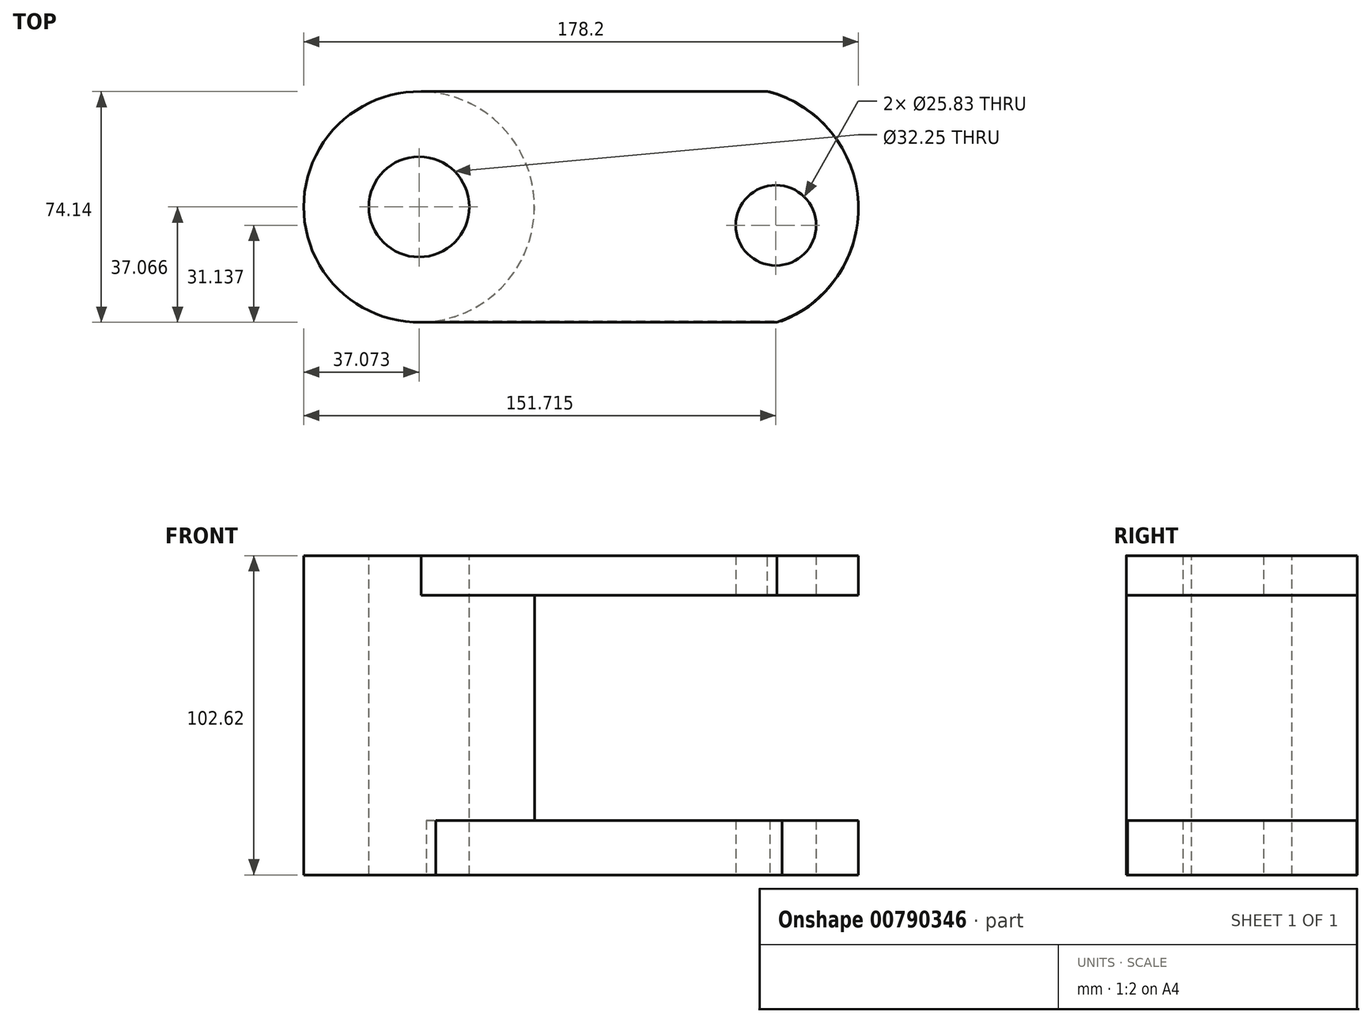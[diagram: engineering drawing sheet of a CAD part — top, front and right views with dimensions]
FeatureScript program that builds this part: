
annotation { "Feature Type Name" : "Feature", "Feature Type Description" : "" }
export const myFeature = defineFeature(function(context is Context, id is Id, definition is map)
    precondition{}
    {
        {
            var Q0;
            Q0=qCreatedBy(makeId("Top.planeOp"),FACE);
            var sketch = newSketch(context, id + "F0", { "sketchPlane" : qUnion([Q0])});
            skCircle(sketch, "E0", {"center": v(-39.45, -5.96) * mm, "radius": 37.07 * mm});
            skSolve(sketch);
        }
        {
            var Q0;
            Q0=makeQuery(id+"F0.imprint","IMPRINT",FACE,{"disambiguationData":[TD([[makeQuery(id+"F0.imprint","IMPRINT",EDGE,{"derivedFrom":sQuery(id+"F0.wireOp",EDGE,"E0")}),1.0]])]});
            extrude(context, id + "F1", {"entities" : qUnion([Q0]), "depth" : 102.62 * mm, "offsetDistance" : 25.4 * mm});
        }
        {
            var Q0;
            Q0=makeQuery(id+"F1.opExtrude","CAP_FACE",FACE,{"disambiguationData":[OSD([sQuery(id+"F0.wireOp",EDGE,"E0")])],"isStart":false});
            var sketch = newSketch(context, id + "F2", { "sketchPlane" : qUnion([Q0])});
            skCircle(sketch, "E1", {"center": v(-39.45, -5.96) * mm, "radius": 16.13 * mm});
            skSolve(sketch);
        }
        {
            var Q0;
            Q0=makeQuery(id+"F2.imprint","IMPRINT",FACE,{"disambiguationData":[TD([[makeQuery(id+"F2.imprint","IMPRINT",EDGE,{"derivedFrom":sQuery(id+"F2.wireOp",EDGE,"E1")}),1.0]])]});
            extrude(context, id + "F3", {"entities" : qUnion([Q0]), "operationType" : NewBodyOperationType.REMOVE, "oppositeDirection" : true, "depth" : 147.83 * mm, "offsetDistance" : 25.4 * mm});
        }
        {
            var Q0;
            Q0=makeQuery(id+"F1.opExtrude","CAP_FACE",FACE,{"disambiguationData":[OSD([sQuery(id+"F0.wireOp",EDGE,"E0")])],"isStart":false});
            var sketch = newSketch(context, id + "F4", { "sketchPlane" : qUnion([Q0])});
            skLineSegment(sketch, "E2", {"start": v(-40.11, 31.1) * mm, "end": v(72.5, 31.1) * mm});
            skLineSegment(sketch, "E3", {"start": v(-40.11, -43.03) * mm, "end": v(75.53, -43.03) * mm});
            skArc(sketch, "E4", {"start": v(75.53, -43.03) * mm, "mid": v(101.65, -4.84) * mm, "end": v(72.5, 31.1) * mm});
            skSolve(sketch);
        }
        {
            var Q0;
            {var subQ0=sQuery(id+"F4.wireOp",EDGE,"E4");Q0=makeQuery(id+"F4.imprint","IMPRINT",FACE,{"disambiguationData":[TD([[makeQuery(id+"F4.imprint","IMPRINT",EDGE,{"derivedFrom":subQ0}),1.0]])]});}
            extrude(context, id + "F5", {"entities" : qUnion([Q0]), "operationType" : NewBodyOperationType.ADD, "oppositeDirection" : true, "depth" : 12.7 * mm, "offsetDistance" : 25.4 * mm});
        }
        {
            var Q0;
            Q0=makeQuery(id+"F1.opExtrude","CAP_FACE",FACE,{"disambiguationData":[OSD([sQuery(id+"F0.wireOp",EDGE,"E0")])],"isStart":true});
            var sketch = newSketch(context, id + "F6", { "sketchPlane" : qUnion([Q0])});
            skLineSegment(sketch, "E5", {"start": v(-34.13, 42.65) * mm, "end": v(77.21, 42.65) * mm});
            skLineSegment(sketch, "E6", {"start": v(-37.13, -31.03) * mm, "end": v(73.18, -31.03) * mm});
            skArc(sketch, "E7", {"start": v(73.18, -31.03) * mm, "mid": v(101.6, 4.36) * mm, "end": v(77.21, 42.65) * mm});
            skSolve(sketch);
        }
        {
            var Q0;
            {var subQ0=sQuery(id+"F6.wireOp",EDGE,"E5");Q0=makeQuery(id+"F6.imprint","IMPRINT",FACE,{"disambiguationData":[TD([[makeQuery(id+"F6.imprint","IMPRINT",EDGE,{"derivedFrom":subQ0}),-1.0]])]});}
            extrude(context, id + "F7", {"entities" : qUnion([Q0]), "operationType" : NewBodyOperationType.ADD, "oppositeDirection" : true, "depth" : 17.53 * mm, "offsetDistance" : 25.4 * mm});
        }
        {
            var Q0;
            {var subQ0=sQuery(id+"F0.wireOp",EDGE,"E0");Q0=makeQuery(id+"F7.boolean.opBoolean","MERGE",FACE,{"derivedFrom":[makeQuery(id+"F1.opExtrude","CAP_FACE",FACE,{"disambiguationData":[OSD([subQ0])],"isStart":true}),makeQuery(id+"F7.opExtrude","CAP_FACE",FACE,{"disambiguationData":[OSD([subQ0,sQuery(id+"F6.wireOp",EDGE,"E5"),sQuery(id+"F6.wireOp",EDGE,"E6"),sQuery(id+"F6.wireOp",EDGE,"E7")])],"isStart":true})]});}
            var sketch = newSketch(context, id + "F8", { "sketchPlane" : qUnion([Q0])});
            skCircle(sketch, "E8", {"center": v(75.2, 11.9) * mm, "radius": 12.91 * mm});
            skSolve(sketch);
        }
        {
            var Q0;
            Q0=makeQuery(id+"F8.imprint","IMPRINT",FACE,{"disambiguationData":[TD([[makeQuery(id+"F8.imprint","IMPRINT",EDGE,{"derivedFrom":sQuery(id+"F8.wireOp",EDGE,"E8")}),1.0]])]});
            extrude(context, id + "F9", {"entities" : qUnion([Q0]), "operationType" : NewBodyOperationType.REMOVE, "oppositeDirection" : true, "depth" : 296.93 * mm, "offsetDistance" : 25.4 * mm});
        }
    });
